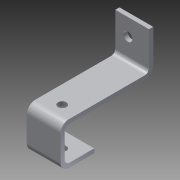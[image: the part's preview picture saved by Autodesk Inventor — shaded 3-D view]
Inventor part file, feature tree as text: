
AUTODESK INVENTOR PART (.ipt)
format: ipt  version: 2013 (Build 170138000, 138)  size: 216,576 bytes
history: native  units: in
note: dims shown in document units (in); Inventor stores cm internally (conversion verified against a paired STEP export)
features: sheet_metal_op x10, other x6, sketch x5, extrude x1, reference x1
ambient origin geometry x8: Origin, YZ Plane, XZ Plane, XY Plane, X Axis, Y Axis, Z Axis, Center Point
bodies: Solid1 (feature_tree)
feature tree (23):
  sheet_metal_op  "Face1"
  sheet_metal_op  "Flange1"
  sheet_metal_op  "Flange2"
  sheet_metal_op  "Flange3"
  extrude  "Extrusion1"  Depth=0.125in
  sketch  "Sketch1"  dims[d0=0.125in d1=0.125in]
  other  "Plate1"
  sketch  "Sketch2"  dims[d2=0.0625in]
  other  "Plate2"
  sheet_metal_op  "Bend1"
  sheet_metal_op  "Corner1"
  sketch  "Sketch3"  dims[d3=0.25in]
  other  "Plate3"
  sheet_metal_op  "Bend2"
  sheet_metal_op  "Corner2"
  sketch  "Sketch4"  dims[d4=0.125in]
  other  "Plate4"
  sheet_metal_op  "Bend3"
  sheet_metal_op  "Corner3"
  sketch  "Sketch5"  dims[d5=2.5in d6=90.0deg d7=0.125in d8=0.5in d9=0.125in d10=0.125in d11=0.125in d12=0.0625in d13=0.25in d14=0.125in d15=1.0in d16=90.0deg d17=0.125in d18=0.5in d19=0.125in d20=0.125in d21=0.125in d22=0.0625in d23=0.25in d24=0.125in d25=1.0in d26=90.0deg d27=0.125in d28=0.5in d29=0.125in d30=0.125in d31=2.1in d33=1.2784in d34=0.25in d35=1.5in d36=0.0in d37=1.0in d38=0.375in]
  reference  "Reference1"
  other  "Definition1"
  other  "Cut1"
